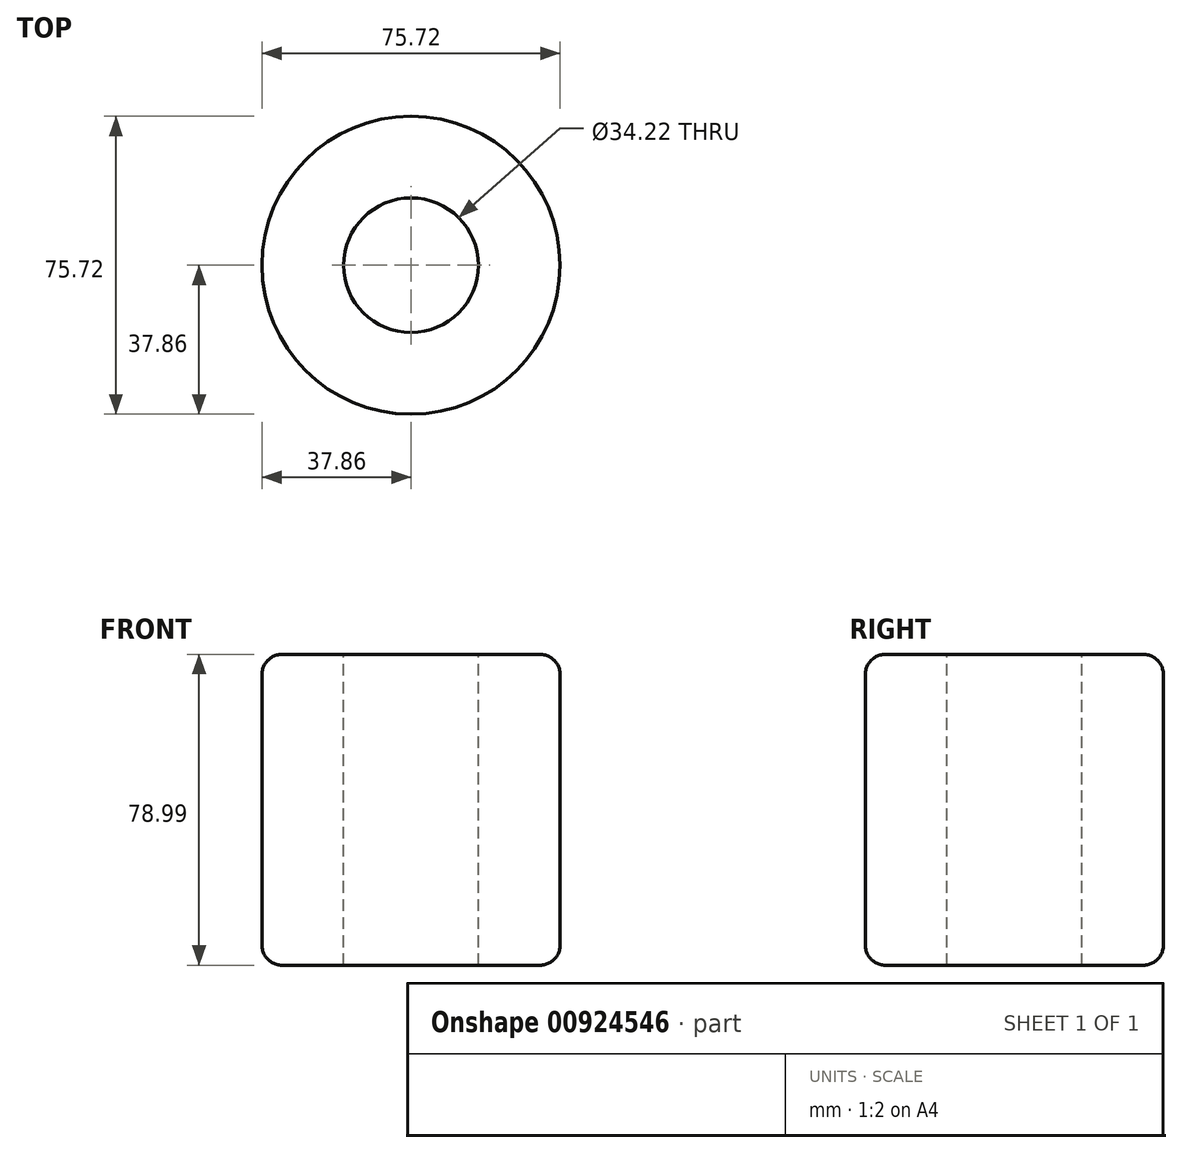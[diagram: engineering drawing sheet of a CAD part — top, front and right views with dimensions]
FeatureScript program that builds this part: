
annotation { "Feature Type Name" : "Feature", "Feature Type Description" : "" }
export const myFeature = defineFeature(function(context is Context, id is Id, definition is map)
    precondition{}
    {
        {
            var Q0;
            Q0=qCreatedBy(makeId("Top.planeOp"),FACE);
            var sketch = newSketch(context, id + "F0", { "sketchPlane" : qUnion([Q0])});
            skCircle(sketch, "E0", {"center": v(0, 0) * mm, "radius": 37.86 * mm});
            skSolve(sketch);
        }
        {
            var Q0;
            Q0=makeQuery(id+"F0.imprint","IMPRINT",FACE,{"disambiguationData":[TD([[makeQuery(id+"F0.imprint","IMPRINT",EDGE,{"derivedFrom":sQuery(id+"F0.wireOp",EDGE,"E0")}),1.0]])]});
            extrude(context, id + "F1", {"entities" : qUnion([Q0]), "depth" : 79 * mm, "offsetDistance" : 25.4 * mm});
        }
        {
            var Q0;
            Q0=makeQuery(id+"F1.opExtrude","SWEPT_FACE",FACE,{"disambiguationData":[OSD([sQuery(id+"F0.wireOp",EDGE,"E0")])]});
            var Q1;
            Q1=makeQuery(id+"F1.opExtrude","CAP_EDGE",EDGE,{"disambiguationData":[OSD([sQuery(id+"F0.wireOp",EDGE,"E0")])],"isStart":false});
            var Q2;
            Q2=makeQuery(id+"F1.opExtrude","CAP_EDGE",EDGE,{"disambiguationData":[OSD([sQuery(id+"F0.wireOp",EDGE,"E0")])],"isStart":true});
            fillet(context, id + "F2", {"entities" : qUnion([Q0, Q1, Q2]), "radius" : 5.08 * mm, "tangentPropagation" : true, "allowEdgeOverflow" : false});
        }
        {
            var Q0;
            Q0=makeQuery(id+"F1.opExtrude","CAP_FACE",FACE,{"disambiguationData":[OSD([sQuery(id+"F0.wireOp",EDGE,"E0")])],"isStart":false});
            var sketch = newSketch(context, id + "F3", { "sketchPlane" : qUnion([Q0])});
            skCircle(sketch, "E1", {"center": v(0, 0) * mm, "radius": 17.1 * mm});
            skSolve(sketch);
        }
        {
            var Q0;
            Q0=makeQuery(id+"F3.imprint","IMPRINT",FACE,{"disambiguationData":[TD([[makeQuery(id+"F3.imprint","IMPRINT",EDGE,{"derivedFrom":sQuery(id+"F3.wireOp",EDGE,"E1")}),1.0]])]});
            extrude(context, id + "F4", {"entities" : qUnion([Q0]), "operationType" : NewBodyOperationType.REMOVE, "oppositeDirection" : true, "depth" : 118.1 * mm, "offsetDistance" : 25.4 * mm});
        }
    });
